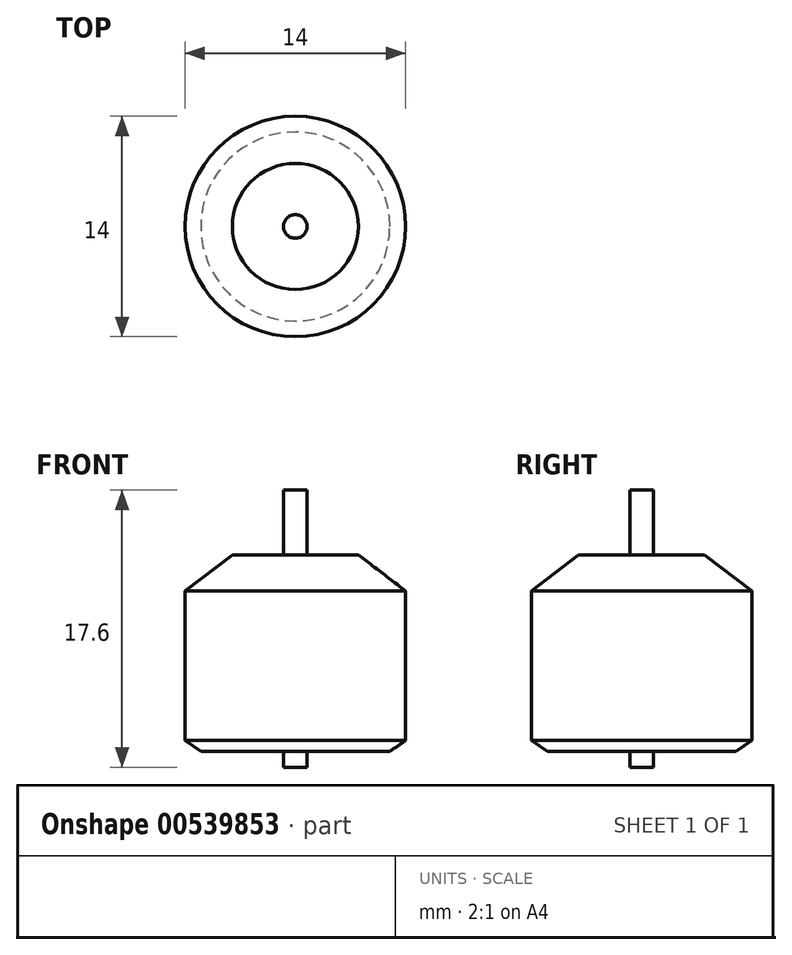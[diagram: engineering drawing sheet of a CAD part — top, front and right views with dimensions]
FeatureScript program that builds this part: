
annotation { "Feature Type Name" : "Feature", "Feature Type Description" : "" }
export const myFeature = defineFeature(function(context is Context, id is Id, definition is map)
    precondition{}
    {
        {
            var Q0;
            Q0=qCreatedBy(makeId("Right.planeOp"),FACE);
            var sketch = newSketch(context, id + "F0", { "sketchPlane" : qUnion([Q0])});
            skLineSegment(sketch, "E0", {"start": v(0, 2.64) * mm, "end": v(0, 0) * mm});
            skLineSegment(sketch, "E1", {"start": v(0, 0) * mm, "end": v(0.75, 0) * mm});
            skLineSegment(sketch, "E2", {"start": v(0.75, 0) * mm, "end": v(0.75, 1) * mm});
            skLineSegment(sketch, "E3", {"start": v(0.75, 1) * mm, "end": v(6, 1) * mm});
            skLineSegment(sketch, "E4", {"start": v(6, 1) * mm, "end": v(7, 1.7) * mm});
            skLineSegment(sketch, "E5", {"start": v(7, 1.7) * mm, "end": v(7, 11.2) * mm});
            skLineSegment(sketch, "E6", {"start": v(7, 11.2) * mm, "end": v(4, 13.5) * mm});
            skLineSegment(sketch, "E7", {"start": v(4, 13.5) * mm, "end": v(0.75, 13.5) * mm});
            skLineSegment(sketch, "E8", {"start": v(0.75, 13.5) * mm, "end": v(0.75, 17.6) * mm});
            skLineSegment(sketch, "E9", {"start": v(0.75, 17.6) * mm, "end": v(0, 17.6) * mm});
            skLineSegment(sketch, "E10", {"start": v(0, 17.6) * mm, "end": v(0, 2.64) * mm});
            skSolve(sketch);
        }
        {
            var Q0;
            Q0=makeQuery(id+"F0.imprint","IMPRINT",FACE,{"disambiguationData":[TD([[makeQuery(id+"F0.imprint","IMPRINT",EDGE,{"derivedFrom":sQuery(id+"F0.wireOp",EDGE,"E0")}),1.0]])]});
            var Q1;
            Q1=sQuery(id+"F0.wireOp",EDGE,"E10");
            revolve(context, id + "F1", {"entities" : qUnion([Q0]), "axis" : qUnion([Q1]), "revolveType" : RevolveType.FULL});
        }
    });
